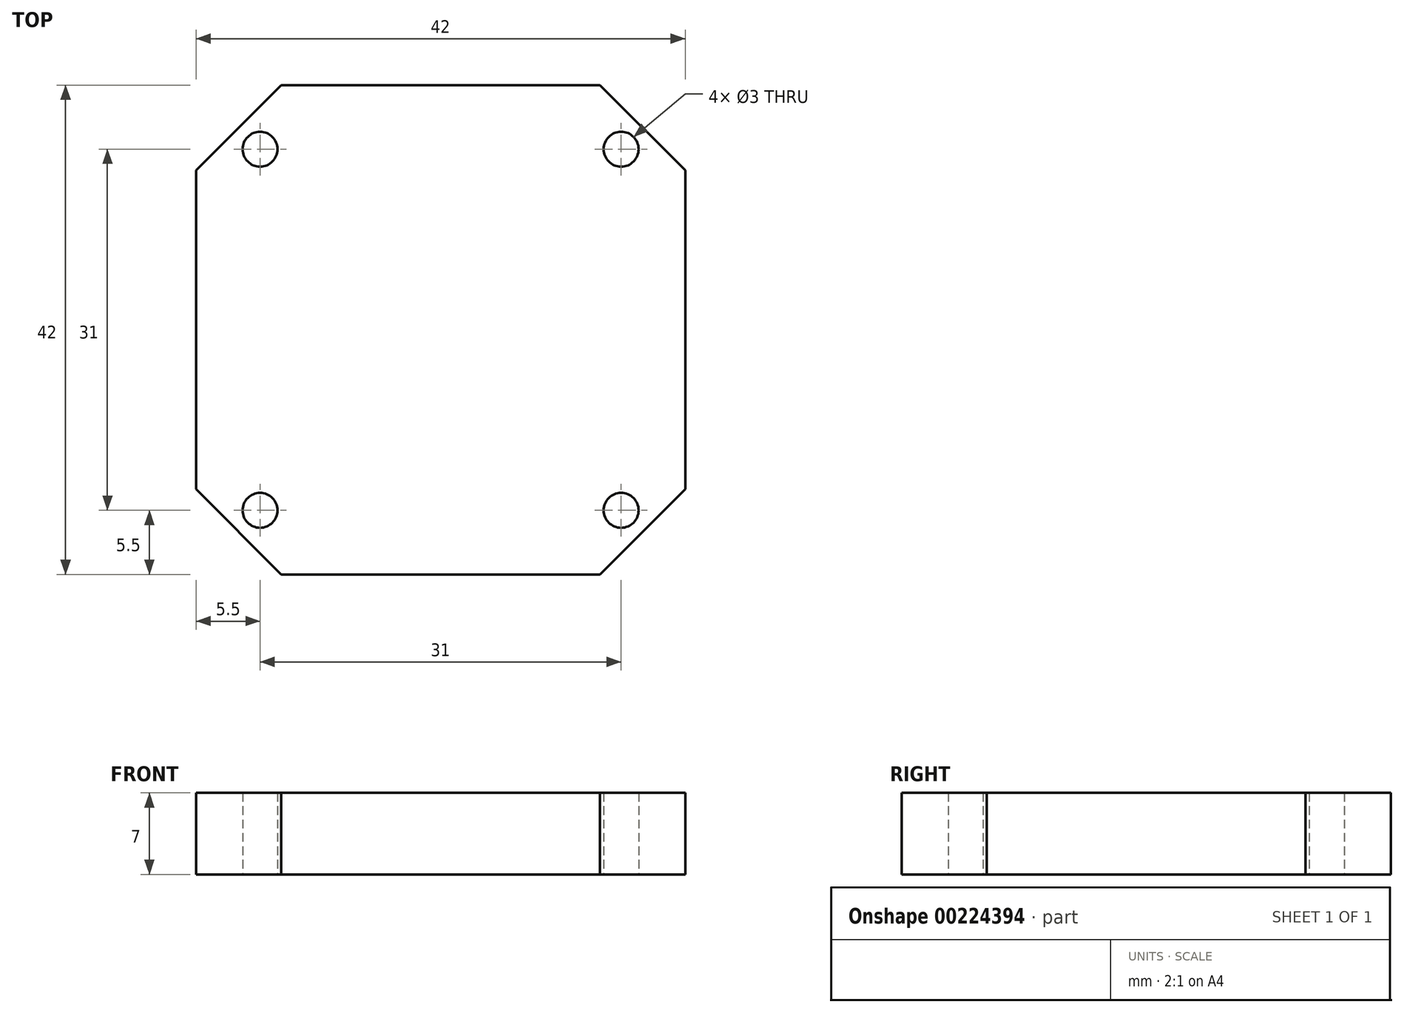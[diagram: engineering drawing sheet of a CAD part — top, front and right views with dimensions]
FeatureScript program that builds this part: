
annotation { "Feature Type Name" : "Feature", "Feature Type Description" : "" }
export const myFeature = defineFeature(function(context is Context, id is Id, definition is map)
    precondition{}
    {
        {
            var Q0;
            Q0=qCreatedBy(makeId("Top.planeOp"),FACE);
            var sketch = newSketch(context, id + "F0", { "sketchPlane" : qUnion([Q0])});
            skLineSegment(sketch, "E0.bottom", {"start": v(21, 21) * mm, "end": v(-21, 21) * mm});
            skLineSegment(sketch, "E0.top", {"start": v(21, -21) * mm, "end": v(-21, -21) * mm});
            skLineSegment(sketch, "E0.left", {"start": v(21, 21) * mm, "end": v(21, -21) * mm});
            skLineSegment(sketch, "E0.right", {"start": v(-21, 21) * mm, "end": v(-21, -21) * mm});
            skPoint(sketch, "E0.middle", {"position": v(0, 0) * mm});
            skLineSegment(sketch, "E1.bottom", {"start": v(15.5, 15.5) * mm, "end": v(-15.5, 15.5) * mm, "construction": true});
            skLineSegment(sketch, "E1.top", {"start": v(15.5, -15.5) * mm, "end": v(-15.5, -15.5) * mm, "construction": true});
            skLineSegment(sketch, "E1.left", {"start": v(15.5, 15.5) * mm, "end": v(15.5, -15.5) * mm, "construction": true});
            skLineSegment(sketch, "E1.right", {"start": v(-15.5, 15.5) * mm, "end": v(-15.5, -15.5) * mm, "construction": true});
            skSolve(sketch);
        }
        {
            var Q0;
            Q0=makeQuery(id+"F0.imprint","IMPRINT",FACE,{"disambiguationData":[TD([[makeQuery(id+"F0.imprint","IMPRINT",EDGE,{"derivedFrom":sQuery(id+"F0.wireOp",EDGE,"E0.bottom")}),1.0]])]});
            extrude(context, id + "F1", {"entities" : qUnion([Q0]), "depth" : 7 * mm});
        }
        {
            var Q0;
            Q0=makeQuery(id+"F1.opExtrude","SWEPT_EDGE",EDGE,{"disambiguationData":[OSD([sQuery(id+"F0.wireOp",EDGE,"E0.top"),sQuery(id+"F0.wireOp",EDGE,"E0.right")])]});
            var Q1;
            Q1=makeQuery(id+"F1.opExtrude","SWEPT_EDGE",EDGE,{"disambiguationData":[OSD([sQuery(id+"F0.wireOp",EDGE,"E0.top"),sQuery(id+"F0.wireOp",EDGE,"E0.left")])]});
            var Q2;
            Q2=makeQuery(id+"F1.opExtrude","SWEPT_EDGE",EDGE,{"disambiguationData":[OSD([sQuery(id+"F0.wireOp",EDGE,"E0.bottom"),sQuery(id+"F0.wireOp",EDGE,"E0.left")])]});
            var Q3;
            Q3=makeQuery(id+"F1.opExtrude","SWEPT_EDGE",EDGE,{"disambiguationData":[OSD([sQuery(id+"F0.wireOp",EDGE,"E0.bottom"),sQuery(id+"F0.wireOp",EDGE,"E0.right")])]});
            chamfer(context, id + "F2", {"entities" : qUnion([Q0, Q1, Q2, Q3]), "width" : 7.33 * mm, "tangentPropagation" : true});
        }
        {
            var Q0;
            Q0=sQuery(id+"F0.wireOp",VERTEX,"E1.left.start");
            var Q1;
            Q1=sQuery(id+"F0.wireOp",VERTEX,"E1.bottom.end");
            var Q2;
            Q2=sQuery(id+"F0.wireOp",VERTEX,"E1.top.end");
            var Q3;
            Q3=sQuery(id+"F0.wireOp",VERTEX,"E1.top.start");
            var Q4;
            Q4=makeQuery(id+"F1.opExtrude","SWEPT_BODY",BODY,{"disambiguationData":[OSD([sQuery(id+"F0.wireOp",EDGE,"E0.bottom"),sQuery(id+"F0.wireOp",EDGE,"E0.top"),sQuery(id+"F0.wireOp",EDGE,"E0.left"),sQuery(id+"F0.wireOp",EDGE,"E0.right")])]});
            hole(context, id + "F3", {"style" : HoleStyle.SIMPLE, "endStyle" : HoleEndStyle.THROUGH, "oppositeDirection" : true, "holeDiameter" : 3 * mm, "locations" : qUnion([Q0, Q1, Q2, Q3]), "scope" : qUnion([Q4]), "isTappedThrough" : true});
        }
    });
